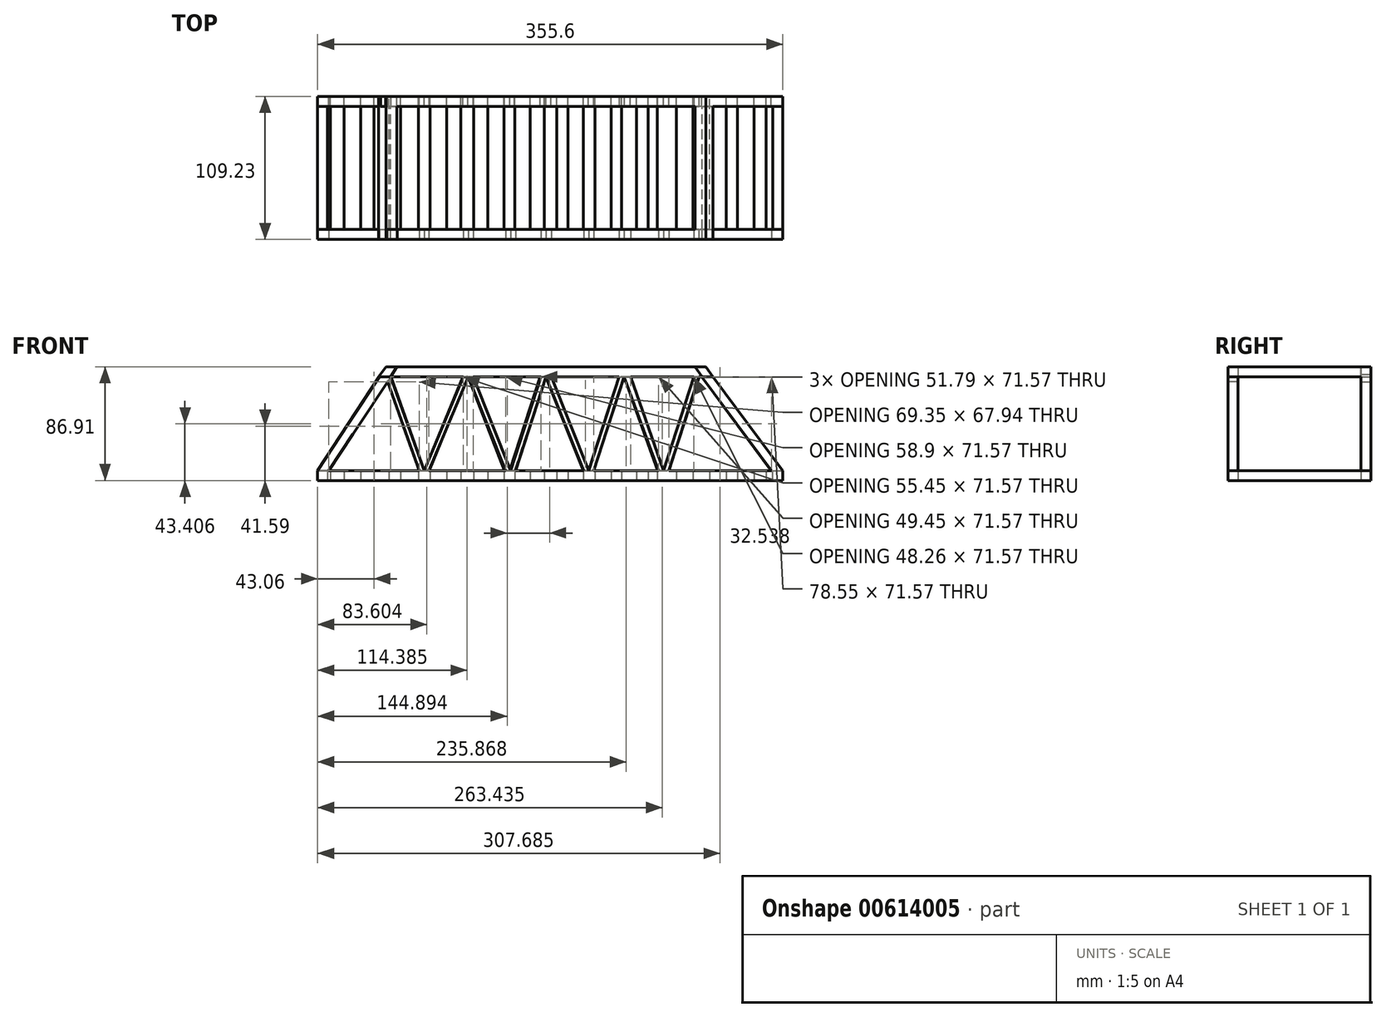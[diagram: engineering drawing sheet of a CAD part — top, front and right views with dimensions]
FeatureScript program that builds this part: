
annotation { "Feature Type Name" : "Feature", "Feature Type Description" : "" }
export const myFeature = defineFeature(function(context is Context, id is Id, definition is map)
    precondition{}
    {
        {
            var Q0;
            Q0=qCreatedBy(makeId("Front.planeOp"),FACE);
            var sketch = newSketch(context, id + "F0", { "sketchPlane" : qUnion([Q0])});
            skLineSegment(sketch, "E0.bottom", {"start": v(-81.44, 46.17) * mm, "end": v(274.16, 46.17) * mm});
            skLineSegment(sketch, "E0.top", {"start": v(-81.44, 38.55) * mm, "end": v(274.16, 38.55) * mm});
            skLineSegment(sketch, "E0.left", {"start": v(-81.44, 46.17) * mm, "end": v(-81.44, 38.55) * mm});
            skLineSegment(sketch, "E0.right", {"start": v(274.16, 46.17) * mm, "end": v(274.16, 38.55) * mm});
            skLineSegment(sketch, "E1.bottom", {"start": v(-81.44, -33.02) * mm, "end": v(274.16, -33.02) * mm});
            skLineSegment(sketch, "E1.top", {"start": v(-81.44, -40.64) * mm, "end": v(274.16, -40.64) * mm});
            skLineSegment(sketch, "E1.left", {"start": v(-81.44, -33.02) * mm, "end": v(-81.44, -40.64) * mm});
            skLineSegment(sketch, "E1.right", {"start": v(274.16, -33.02) * mm, "end": v(274.16, -40.64) * mm});
            skSolve(sketch);
        }
        {
            var Q0;
            Q0=makeQuery(id+"F0.imprint","IMPRINT",FACE,{"disambiguationData":[TD([[makeQuery(id+"F0.imprint","IMPRINT",EDGE,{"derivedFrom":sQuery(id+"F0.wireOp",EDGE,"E0.bottom")}),-1.0]])]});
            var Q1;
            Q1=makeQuery(id+"F0.imprint","IMPRINT",FACE,{"disambiguationData":[TD([[makeQuery(id+"F0.imprint","IMPRINT",EDGE,{"derivedFrom":sQuery(id+"F0.wireOp",EDGE,"E1.bottom")}),-1.0]])]});
            extrude(context, id + "F1", {"entities" : qUnion([Q0, Q1]), "depth" : 7.62 * mm, "offsetDistance" : 25.4 * mm});
        }
        {
            var Q0;
            Q0=makeQuery(id+"F1.opExtrude","SWEPT_FACE",FACE,{"disambiguationData":[OSD([sQuery(id+"F0.wireOp",EDGE,"E1.left")])]});
            var sketch = newSketch(context, id + "F2", { "sketchPlane" : qUnion([Q0])});
            skLineSegment(sketch, "E2.bottom", {"start": v(7.62, -33.02) * mm, "end": v(-101.6, -33.02) * mm});
            skLineSegment(sketch, "E2.top", {"start": v(7.62, -40.64) * mm, "end": v(-101.6, -40.64) * mm});
            skLineSegment(sketch, "E2.left", {"start": v(7.62, -33.02) * mm, "end": v(7.62, -40.64) * mm});
            skLineSegment(sketch, "E2.right", {"start": v(-101.6, -33.02) * mm, "end": v(-101.6, -40.64) * mm});
            skSolve(sketch);
        }
        {
            var Q0;
            Q0 = qSketchRegion(id + "F2", true);
            extrude(context, id + "F3", {"entities" : qUnion([Q0]), "operationType" : NewBodyOperationType.ADD, "oppositeDirection" : true, "depth" : 7.62 * mm, "offsetDistance" : 25.4 * mm});
        }
        {
            var Q0;
            Q0=makeQuery(id+"F1.opExtrude","CAP_FACE",FACE,{"disambiguationData":[OSD([sQuery(id+"F0.wireOp",EDGE,"E0.bottom"),sQuery(id+"F0.wireOp",EDGE,"E0.top"),sQuery(id+"F0.wireOp",EDGE,"E0.left"),sQuery(id+"F0.wireOp",EDGE,"E0.right")])],"isStart":true});
            var sketch = newSketch(context, id + "F4", { "sketchPlane" : qUnion([Q0])});
            skLineSegment(sketch, "E3.bottom", {"start": v(81.44, 46.17) * mm, "end": v(73.82, 46.17) * mm});
            skLineSegment(sketch, "E3.top", {"start": v(81.44, 38.55) * mm, "end": v(73.82, 38.55) * mm});
            skLineSegment(sketch, "E3.left", {"start": v(81.44, 46.17) * mm, "end": v(81.44, 38.55) * mm});
            skLineSegment(sketch, "E3.right", {"start": v(73.82, 46.17) * mm, "end": v(73.82, 38.55) * mm});
            skSolve(sketch);
        }
        {
            var Q0;
            Q0 = qSketchRegion(id + "F4", true);
            extrude(context, id + "F5", {"entities" : qUnion([Q0]), "operationType" : NewBodyOperationType.ADD, "depth" : 101.6 * mm, "offsetDistance" : 25.4 * mm});
        }
        {
            var Q0;
            Q0=makeQuery(id+"F5.opExtrude","SWEPT_FACE",FACE,{"disambiguationData":[OSD([sQuery(id+"F4.wireOp",EDGE,"E3.right")])]});
            var sketch = newSketch(context, id + "F6", { "sketchPlane" : qUnion([Q0])});
            skLineSegment(sketch, "E4.bottom", {"start": v(101.6, 46.17) * mm, "end": v(93.97, 46.17) * mm});
            skLineSegment(sketch, "E4.top", {"start": v(101.6, 38.55) * mm, "end": v(93.97, 38.55) * mm});
            skLineSegment(sketch, "E4.left", {"start": v(101.6, 46.17) * mm, "end": v(101.6, 38.55) * mm});
            skLineSegment(sketch, "E4.right", {"start": v(93.97, 46.17) * mm, "end": v(93.97, 38.55) * mm});
            skSolve(sketch);
        }
        {
            var Q0;
            Q0 = qSketchRegion(id + "F6", true);
            extrude(context, id + "F7", {"entities" : qUnion([Q0]), "operationType" : NewBodyOperationType.ADD, "depth" : 347.98 * mm, "offsetDistance" : 25.4 * mm});
        }
        {
            var Q0;
            Q0=makeQuery(id+"F1.opExtrude","CAP_FACE",FACE,{"disambiguationData":[OSD([sQuery(id+"F0.wireOp",EDGE,"E0.bottom"),sQuery(id+"F0.wireOp",EDGE,"E0.top"),sQuery(id+"F0.wireOp",EDGE,"E0.left"),sQuery(id+"F0.wireOp",EDGE,"E0.right")])],"isStart":true});
            var sketch = newSketch(context, id + "F8", { "sketchPlane" : qUnion([Q0])});
            skLineSegment(sketch, "E5.bottom", {"start": v(-274.16, 46.17) * mm, "end": v(-266.54, 46.17) * mm});
            skLineSegment(sketch, "E5.top", {"start": v(-274.16, 38.55) * mm, "end": v(-266.54, 38.55) * mm});
            skLineSegment(sketch, "E5.left", {"start": v(-274.16, 46.17) * mm, "end": v(-274.16, 38.55) * mm});
            skLineSegment(sketch, "E5.right", {"start": v(-266.54, 46.17) * mm, "end": v(-266.54, 38.55) * mm});
            skSolve(sketch);
        }
        {
            var Q0;
            Q0 = qSketchRegion(id + "F8", true);
            extrude(context, id + "F9", {"entities" : qUnion([Q0]), "operationType" : NewBodyOperationType.ADD, "depth" : 93.98 * mm, "offsetDistance" : 25.4 * mm});
        }
        {
            var Q0;
            Q0=makeQuery(id+"F1.opExtrude","CAP_FACE",FACE,{"disambiguationData":[OSD([sQuery(id+"F0.wireOp",EDGE,"E1.bottom"),sQuery(id+"F0.wireOp",EDGE,"E1.top"),sQuery(id+"F0.wireOp",EDGE,"E1.left"),sQuery(id+"F0.wireOp",EDGE,"E1.right")])],"isStart":true});
            var sketch = newSketch(context, id + "F10", { "sketchPlane" : qUnion([Q0])});
            skLineSegment(sketch, "E6.bottom", {"start": v(-274.16, -40.64) * mm, "end": v(-266.54, -40.64) * mm});
            skLineSegment(sketch, "E6.top", {"start": v(-274.16, -33.02) * mm, "end": v(-266.54, -33.02) * mm});
            skLineSegment(sketch, "E6.left", {"start": v(-274.16, -40.64) * mm, "end": v(-274.16, -33.02) * mm});
            skLineSegment(sketch, "E6.right", {"start": v(-266.54, -40.64) * mm, "end": v(-266.54, -33.02) * mm});
            skSolve(sketch);
        }
        {
            var Q0;
            Q0 = qSketchRegion(id + "F10", true);
            extrude(context, id + "F11", {"entities" : qUnion([Q0]), "operationType" : NewBodyOperationType.ADD, "depth" : 101.6 * mm, "offsetDistance" : 25.4 * mm});
        }
        {
            var Q0;
            Q0=makeQuery(id+"F11.opExtrude","SWEPT_FACE",FACE,{"disambiguationData":[OSD([sQuery(id+"F10.wireOp",EDGE,"E6.right")])]});
            var sketch = newSketch(context, id + "F12", { "sketchPlane" : qUnion([Q0])});
            skLineSegment(sketch, "E7.bottom", {"start": v(-101.6, -33.02) * mm, "end": v(-93.98, -33.02) * mm});
            skLineSegment(sketch, "E7.top", {"start": v(-101.6, -40.64) * mm, "end": v(-93.98, -40.64) * mm});
            skLineSegment(sketch, "E7.left", {"start": v(-101.6, -33.02) * mm, "end": v(-101.6, -40.64) * mm});
            skLineSegment(sketch, "E7.right", {"start": v(-93.98, -33.02) * mm, "end": v(-93.98, -40.64) * mm});
            skSolve(sketch);
        }
        {
            var Q0;
            Q0 = qSketchRegion(id + "F12", true);
            extrude(context, id + "F13", {"entities" : qUnion([Q0]), "operationType" : NewBodyOperationType.ADD, "depth" : 340.36 * mm, "offsetDistance" : 25.4 * mm});
        }
        {
            var Q0;
            Q0=makeQuery(id+"F1.opExtrude","CAP_FACE",FACE,{"disambiguationData":[OSD([sQuery(id+"F0.wireOp",EDGE,"E1.bottom"),sQuery(id+"F0.wireOp",EDGE,"E1.top"),sQuery(id+"F0.wireOp",EDGE,"E1.left"),sQuery(id+"F0.wireOp",EDGE,"E1.right")])],"isStart":false});
            var sketch = newSketch(context, id + "F14", { "sketchPlane" : qUnion([Q0])});
            skLineSegment(sketch, "E8", {"start": v(-81.44, -33.02) * mm, "end": v(-28.78, 46.35) * mm});
            skLineSegment(sketch, "E9", {"start": v(-28.78, 46.35) * mm, "end": v(-20.39, 46.35) * mm});
            skLineSegment(sketch, "E10", {"start": v(-20.39, 46.35) * mm, "end": v(-73.05, -33.02) * mm});
            skLineSegment(sketch, "E11", {"start": v(-73.05, -33.02) * mm, "end": v(-81.44, -33.02) * mm});
            skSolve(sketch);
        }
        {
            var Q0;
            Q0=makeQuery(id+"F14.imprint","IMPRINT",FACE,{"disambiguationData":[TD([[makeQuery(id+"F14.imprint","IMPRINT",EDGE,{"derivedFrom":sQuery(id+"F14.wireOp",EDGE,"E8")}),-1.0]])]});
            extrude(context, id + "F15", {"entities" : qUnion([Q0]), "oppositeDirection" : true, "depth" : 7.62 * mm, "offsetDistance" : 25.4 * mm});
        }
        {
            var Q0;
            Q0=makeQuery(id+"F15.opExtrude","SWEPT_BODY",BODY,{"disambiguationData":[OSD([sQuery(id+"F14.wireOp",EDGE,"E8"),sQuery(id+"F14.wireOp",EDGE,"E9"),sQuery(id+"F14.wireOp",EDGE,"E10"),sQuery(id+"F14.wireOp",EDGE,"E11")])]});
            var Q1;
            Q1=makeQuery(id+"F1.opExtrude","SWEPT_BODY",BODY,{"disambiguationData":[OSD([sQuery(id+"F0.wireOp",EDGE,"E0.bottom"),sQuery(id+"F0.wireOp",EDGE,"E0.top"),sQuery(id+"F0.wireOp",EDGE,"E0.left"),sQuery(id+"F0.wireOp",EDGE,"E0.right")])]});
            booleanBodies(context, id + "F16", {"operationType" : BooleanOperationType.UNION, "tools" : qUnion([Q0, Q1])});
        }
        {
            var Q0;
            Q0=makeQuery(id+"F16.opBoolean","MERGE",FACE,{"derivedFrom":[makeQuery(id+"F1.opExtrude","CAP_FACE",FACE,{"disambiguationData":[OSD([sQuery(id+"F0.wireOp",EDGE,"E0.bottom"),sQuery(id+"F0.wireOp",EDGE,"E0.top"),sQuery(id+"F0.wireOp",EDGE,"E0.left"),sQuery(id+"F0.wireOp",EDGE,"E0.right")])],"isStart":false}),makeQuery(id+"F15.opExtrude","CAP_FACE",FACE,{"disambiguationData":[OSD([sQuery(id+"F14.wireOp",EDGE,"E8"),sQuery(id+"F14.wireOp",EDGE,"E9"),sQuery(id+"F14.wireOp",EDGE,"E10"),sQuery(id+"F14.wireOp",EDGE,"E11")])],"isStart":true})]});
            var sketch = newSketch(context, id + "F17", { "sketchPlane" : qUnion([Q0])});
            skLineSegment(sketch, "E12", {"start": v(-33.95, 38.55) * mm, "end": v(-28.78, 46.35) * mm});
            skLineSegment(sketch, "E13", {"start": v(-28.78, 46.35) * mm, "end": v(-81.44, 46.17) * mm});
            skLineSegment(sketch, "E14", {"start": v(-81.44, 46.17) * mm, "end": v(-81.44, 38.55) * mm});
            skLineSegment(sketch, "E15", {"start": v(-81.44, 38.55) * mm, "end": v(-33.95, 38.55) * mm});
            skSolve(sketch);
        }
        {
            var Q0;
            Q0=makeQuery(id+"F13.boolean.opBoolean","MERGE",FACE,{"derivedFrom":[makeQuery(id+"F3.opExtrude","SWEPT_FACE",FACE,{"disambiguationData":[OSD([sQuery(id+"F2.wireOp",EDGE,"E2.right")])]}),makeQuery(id+"F11.opExtrude","CAP_FACE",FACE,{"disambiguationData":[OSD([sQuery(id+"F10.wireOp",EDGE,"E6.bottom"),sQuery(id+"F10.wireOp",EDGE,"E6.top"),sQuery(id+"F10.wireOp",EDGE,"E6.left"),sQuery(id+"F10.wireOp",EDGE,"E6.right")])],"isStart":false}),makeQuery(id+"F13.opExtrude","SWEPT_FACE",FACE,{"disambiguationData":[OSD([sQuery(id+"F12.wireOp",EDGE,"E7.left")])]})]});
            var sketch = newSketch(context, id + "F18", { "sketchPlane" : qUnion([Q0])});
            skLineSegment(sketch, "E16", {"start": v(81.44, -33.02) * mm, "end": v(29.7, 45.88) * mm});
            skLineSegment(sketch, "E17", {"start": v(29.7, 45.88) * mm, "end": v(20.94, 45.88) * mm});
            skLineSegment(sketch, "E18", {"start": v(20.94, 45.88) * mm, "end": v(72.92, -33.02) * mm});
            skLineSegment(sketch, "E19", {"start": v(72.92, -33.02) * mm, "end": v(81.44, -33.02) * mm});
            skSolve(sketch);
        }
        {
            var Q0;
            Q0 = qSketchRegion(id + "F18", true);
            extrude(context, id + "F19", {"entities" : qUnion([Q0]), "oppositeDirection" : true, "depth" : 7.62 * mm, "offsetDistance" : 25.4 * mm});
        }
        {
            var Q0;
            Q0=makeQuery(id+"F17.imprint","IMPRINT",FACE,{"disambiguationData":[TD([[makeQuery(id+"F17.imprint","IMPRINT",EDGE,{"derivedFrom":sQuery(id+"F17.wireOp",EDGE,"E14")}),1.0]])]});
            var sketch = newSketch(context, id + "F20", { "sketchPlane" : qUnion([Q0])});
            skLineSegment(sketch, "E20", {"start": v(-28.75, 46.61) * mm, "end": v(-36.09, 36.61) * mm});
            skLineSegment(sketch, "E21", {"start": v(-36.09, 36.61) * mm, "end": v(-88.6, 34.11) * mm});
            skLineSegment(sketch, "E22", {"start": v(-88.6, 34.11) * mm, "end": v(-88.6, 49.28) * mm});
            skLineSegment(sketch, "E23", {"start": v(-88.6, 49.28) * mm, "end": v(-28.92, 49.28) * mm});
            skLineSegment(sketch, "E24", {"start": v(-28.92, 49.28) * mm, "end": v(-19.25, 49.28) * mm});
            skLineSegment(sketch, "E25", {"start": v(-19.25, 49.28) * mm, "end": v(-19.25, 46.27) * mm});
            skLineSegment(sketch, "E26", {"start": v(-19.25, 46.27) * mm, "end": v(-29, 46.27) * mm});
            skSolve(sketch);
        }
        {
            var Q0;
            Q0 = qSketchRegion(id + "F20", true);
            extrude(context, id + "F21", {"entities" : qUnion([Q0]), "operationType" : NewBodyOperationType.REMOVE, "oppositeDirection" : true, "depth" : 127 * mm, "offsetDistance" : 25.4 * mm});
        }
        {
            var Q0;
            Q0=makeQuery(id+"F17.imprint","IMPRINT",FACE,{"disambiguationData":[TD([[makeQuery(id+"F17.imprint","IMPRINT",EDGE,{"derivedFrom":sQuery(id+"F17.wireOp",EDGE,"E14")}),1.0]])]});
            extrude(context, id + "F22", {"entities" : qUnion([Q0]), "operationType" : NewBodyOperationType.REMOVE, "oppositeDirection" : true, "depth" : 25.4 * mm, "offsetDistance" : 25.4 * mm});
        }
        {
            var Q0;
            Q0=makeQuery(id+"F1.opExtrude","CAP_FACE",FACE,{"disambiguationData":[OSD([sQuery(id+"F0.wireOp",EDGE,"E1.bottom"),sQuery(id+"F0.wireOp",EDGE,"E1.top"),sQuery(id+"F0.wireOp",EDGE,"E1.left"),sQuery(id+"F0.wireOp",EDGE,"E1.right")])],"isStart":false});
            var sketch = newSketch(context, id + "F23", { "sketchPlane" : qUnion([Q0])});
            skLineSegment(sketch, "E27", {"start": v(274.16, -33.02) * mm, "end": v(214.97, 46.19) * mm});
            skLineSegment(sketch, "E28", {"start": v(214.97, 46.19) * mm, "end": v(206.33, 46.19) * mm});
            skLineSegment(sketch, "E29", {"start": v(206.33, 46.19) * mm, "end": v(265.52, -33.02) * mm});
            skLineSegment(sketch, "E30", {"start": v(265.52, -33.02) * mm, "end": v(274.16, -33.02) * mm});
            skSolve(sketch);
        }
        {
            var Q0;
            Q0 = qSketchRegion(id + "F23", true);
            extrude(context, id + "F24", {"entities" : qUnion([Q0]), "operationType" : NewBodyOperationType.ADD, "oppositeDirection" : true, "depth" : 7.62 * mm, "offsetDistance" : 25.4 * mm});
        }
        {
            var Q0;
            Q0=makeQuery(id+"F13.boolean.opBoolean","MERGE",FACE,{"derivedFrom":[makeQuery(id+"F3.opExtrude","SWEPT_FACE",FACE,{"disambiguationData":[OSD([sQuery(id+"F2.wireOp",EDGE,"E2.right")])]}),makeQuery(id+"F11.opExtrude","CAP_FACE",FACE,{"disambiguationData":[OSD([sQuery(id+"F10.wireOp",EDGE,"E6.bottom"),sQuery(id+"F10.wireOp",EDGE,"E6.top"),sQuery(id+"F10.wireOp",EDGE,"E6.left"),sQuery(id+"F10.wireOp",EDGE,"E6.right")])],"isStart":false}),makeQuery(id+"F13.opExtrude","SWEPT_FACE",FACE,{"disambiguationData":[OSD([sQuery(id+"F12.wireOp",EDGE,"E7.left")])]})]});
            var sketch = newSketch(context, id + "F25", { "sketchPlane" : qUnion([Q0])});
            skLineSegment(sketch, "E31", {"start": v(-274.16, -33.02) * mm, "end": v(-214.97, 46.51) * mm});
            skLineSegment(sketch, "E32", {"start": v(-214.97, 46.51) * mm, "end": v(-206.28, 46.51) * mm});
            skLineSegment(sketch, "E33", {"start": v(-206.28, 46.51) * mm, "end": v(-265.18, -33.02) * mm});
            skLineSegment(sketch, "E34", {"start": v(-265.18, -33.02) * mm, "end": v(-274.16, -33.02) * mm});
            skSolve(sketch);
        }
        {
            var Q0;
            Q0 = qSketchRegion(id + "F25", true);
            extrude(context, id + "F26", {"entities" : qUnion([Q0]), "operationType" : NewBodyOperationType.ADD, "oppositeDirection" : true, "depth" : 7.62 * mm, "offsetDistance" : 25.4 * mm});
        }
        {
            var Q0;
            Q0=makeQuery(id+"F26.boolean.opBoolean","MERGE",FACE,{"derivedFrom":[makeQuery(id+"F13.boolean.opBoolean","MERGE",FACE,{"derivedFrom":[makeQuery(id+"F3.opExtrude","SWEPT_FACE",FACE,{"disambiguationData":[OSD([sQuery(id+"F2.wireOp",EDGE,"E2.right")])]}),makeQuery(id+"F11.opExtrude","CAP_FACE",FACE,{"disambiguationData":[OSD([sQuery(id+"F10.wireOp",EDGE,"E6.bottom"),sQuery(id+"F10.wireOp",EDGE,"E6.top"),sQuery(id+"F10.wireOp",EDGE,"E6.left"),sQuery(id+"F10.wireOp",EDGE,"E6.right")])],"isStart":false}),makeQuery(id+"F13.opExtrude","SWEPT_FACE",FACE,{"disambiguationData":[OSD([sQuery(id+"F12.wireOp",EDGE,"E7.left")])]})]}),makeQuery(id+"F7.boolean.opBoolean","MERGE",FACE,{"derivedFrom":[makeQuery(id+"F5.opExtrude","CAP_FACE",FACE,{"disambiguationData":[OSD([sQuery(id+"F4.wireOp",EDGE,"E3.bottom"),sQuery(id+"F4.wireOp",EDGE,"E3.top"),sQuery(id+"F4.wireOp",EDGE,"E3.left"),sQuery(id+"F4.wireOp",EDGE,"E3.right")])],"isStart":false}),makeQuery(id+"F7.opExtrude","SWEPT_FACE",FACE,{"disambiguationData":[OSD([sQuery(id+"F6.wireOp",EDGE,"E4.left")])]})]}),makeQuery(id+"F26.opExtrude","CAP_FACE",FACE,{"disambiguationData":[OSD([sQuery(id+"F25.wireOp",EDGE,"E31"),sQuery(id+"F25.wireOp",EDGE,"E32"),sQuery(id+"F25.wireOp",EDGE,"E33"),sQuery(id+"F25.wireOp",EDGE,"E34")])],"isStart":true})]});
            var sketch = newSketch(context, id + "F27", { "sketchPlane" : qUnion([Q0])});
            skLineSegment(sketch, "E35", {"start": v(-220.9, 38.55) * mm, "end": v(-215.22, 46.17) * mm});
            skLineSegment(sketch, "E36", {"start": v(-215.22, 46.17) * mm, "end": v(-206.2, 46.17) * mm});
            skLineSegment(sketch, "E37", {"start": v(-206.2, 46.17) * mm, "end": v(-206.2, 46.76) * mm});
            skLineSegment(sketch, "E38", {"start": v(-206.2, 46.76) * mm, "end": v(-277.38, 46.17) * mm});
            skLineSegment(sketch, "E39", {"start": v(-277.38, 46.17) * mm, "end": v(-277.38, 38.55) * mm});
            skLineSegment(sketch, "E40", {"start": v(-277.38, 38.55) * mm, "end": v(-220.9, 38.55) * mm});
            skSolve(sketch);
        }
        {
            var Q0;
            Q0 = qSketchRegion(id + "F27", true);
            extrude(context, id + "F28", {"entities" : qUnion([Q0]), "operationType" : NewBodyOperationType.REMOVE, "oppositeDirection" : true, "depth" : 127 * mm, "offsetDistance" : 25.4 * mm});
        }
        {
            var Q0;
            Q0=makeQuery(id+"F24.boolean.opBoolean","MERGE",FACE,{"derivedFrom":[makeQuery(id+"F1.opExtrude","CAP_FACE",FACE,{"disambiguationData":[OSD([sQuery(id+"F0.wireOp",EDGE,"E1.bottom"),sQuery(id+"F0.wireOp",EDGE,"E1.top"),sQuery(id+"F0.wireOp",EDGE,"E1.left"),sQuery(id+"F0.wireOp",EDGE,"E1.right")])],"isStart":false}),makeQuery(id+"F16.opBoolean","MERGE",FACE,{"derivedFrom":[makeQuery(id+"F1.opExtrude","CAP_FACE",FACE,{"disambiguationData":[OSD([sQuery(id+"F0.wireOp",EDGE,"E0.bottom"),sQuery(id+"F0.wireOp",EDGE,"E0.top"),sQuery(id+"F0.wireOp",EDGE,"E0.left"),sQuery(id+"F0.wireOp",EDGE,"E0.right")])],"isStart":false}),makeQuery(id+"F15.opExtrude","CAP_FACE",FACE,{"disambiguationData":[OSD([sQuery(id+"F14.wireOp",EDGE,"E8"),sQuery(id+"F14.wireOp",EDGE,"E9"),sQuery(id+"F14.wireOp",EDGE,"E10"),sQuery(id+"F14.wireOp",EDGE,"E11")])],"isStart":true})]}),makeQuery(id+"F24.opExtrude","CAP_FACE",FACE,{"disambiguationData":[OSD([sQuery(id+"F23.wireOp",EDGE,"E27"),sQuery(id+"F23.wireOp",EDGE,"E28"),sQuery(id+"F23.wireOp",EDGE,"E29"),sQuery(id+"F23.wireOp",EDGE,"E30")])],"isStart":true})]});
            var sketch = newSketch(context, id + "F29", { "sketchPlane" : qUnion([Q0])});
            skLineSegment(sketch, "E41", {"start": v(3.5, -33.02) * mm, "end": v(33.75, 38.55) * mm});
            skLineSegment(sketch, "E42", {"start": v(33.75, 38.55) * mm, "end": v(29.89, 38.55) * mm});
            skLineSegment(sketch, "E43", {"start": v(33.75, 38.55) * mm, "end": v(62.4, -33.02) * mm});
            skLineSegment(sketch, "E44", {"start": v(62.4, -33.02) * mm, "end": v(66.2, -33.02) * mm});
            skLineSegment(sketch, "E45", {"start": v(66.2, -33.02) * mm, "end": v(37.56, 38.55) * mm});
            skLineSegment(sketch, "E46", {"start": v(37.56, 38.55) * mm, "end": v(33.75, 38.55) * mm});
            skLineSegment(sketch, "E47", {"start": v(66.2, -33.02) * mm, "end": v(89.35, 38.55) * mm});
            skLineSegment(sketch, "E48", {"start": v(89.35, 38.55) * mm, "end": v(93.24, 38.55) * mm});
            skLineSegment(sketch, "E49", {"start": v(93.24, 38.55) * mm, "end": v(70.1, -33.02) * mm});
            skLineSegment(sketch, "E50", {"start": v(70.1, -33.02) * mm, "end": v(66.2, -33.02) * mm});
            skLineSegment(sketch, "E51", {"start": v(93.24, 38.55) * mm, "end": v(121.88, -33.02) * mm});
            skLineSegment(sketch, "E52", {"start": v(121.88, -33.02) * mm, "end": v(125.9, -33.02) * mm});
            skLineSegment(sketch, "E53", {"start": v(125.9, -33.02) * mm, "end": v(97.25, 38.55) * mm});
            skLineSegment(sketch, "E54", {"start": v(97.25, 38.55) * mm, "end": v(93.24, 38.55) * mm});
            skLineSegment(sketch, "E55", {"start": v(29.89, 38.55) * mm, "end": v(0, -33.02) * mm});
            skLineSegment(sketch, "E56", {"start": v(0, -33.02) * mm, "end": v(-25.56, 38.55) * mm});
            skLineSegment(sketch, "E57", {"start": v(-25.56, 38.55) * mm, "end": v(-27.97, 34.92) * mm});
            skLineSegment(sketch, "E58", {"start": v(-27.97, 34.92) * mm, "end": v(-3.7, -33.02) * mm});
            skLineSegment(sketch, "E59", {"start": v(-3.7, -33.02) * mm, "end": v(0, -33.02) * mm});
            skLineSegment(sketch, "E60", {"start": v(125.9, -33.02) * mm, "end": v(149.03, 38.55) * mm});
            skLineSegment(sketch, "E61", {"start": v(149.03, 38.55) * mm, "end": v(152.84, 38.55) * mm});
            skLineSegment(sketch, "E62", {"start": v(152.84, 38.55) * mm, "end": v(129.7, -33.02) * mm});
            skLineSegment(sketch, "E63", {"start": v(129.7, -33.02) * mm, "end": v(125.9, -33.02) * mm});
            skLineSegment(sketch, "E64", {"start": v(152.84, 38.55) * mm, "end": v(179.15, -33.02) * mm});
            skLineSegment(sketch, "E65", {"start": v(179.15, -33.02) * mm, "end": v(182.98, -33.02) * mm});
            skLineSegment(sketch, "E66", {"start": v(182.98, -33.02) * mm, "end": v(157.86, 38.55) * mm});
            skLineSegment(sketch, "E67", {"start": v(157.86, 38.55) * mm, "end": v(152.84, 38.55) * mm});
            skLineSegment(sketch, "E68", {"start": v(182.98, -33.02) * mm, "end": v(206.12, 38.55) * mm});
            skLineSegment(sketch, "E69", {"start": v(206.12, 38.55) * mm, "end": v(210.11, 38.55) * mm});
            skLineSegment(sketch, "E70", {"start": v(210.11, 38.55) * mm, "end": v(186.97, -33.02) * mm});
            skLineSegment(sketch, "E71", {"start": v(186.97, -33.02) * mm, "end": v(182.98, -33.02) * mm});
            skLineSegment(sketch, "E72", {"start": v(157.86, 38.55) * mm, "end": v(206.12, 38.55) * mm});
            skSolve(sketch);
        }
        {
            var Q0;
            Q0=makeQuery(id+"F29.imprint","IMPRINT",FACE,{"disambiguationData":[TD([[makeQuery(id+"F29.imprint","IMPRINT",EDGE,{"derivedFrom":sQuery(id+"F29.wireOp",EDGE,"E56")}),1.0]])]});
            var Q1;
            {var subQ0=sQuery(id+"F29.wireOp",EDGE,"E41");Q1=makeQuery(id+"F29.imprint","IMPRINT",FACE,{"disambiguationData":[TD([[makeQuery(id+"F29.imprint","IMPRINT",EDGE,{"derivedFrom":subQ0}),1.0]])]});}
            var Q2;
            Q2=makeQuery(id+"F29.imprint","IMPRINT",FACE,{"disambiguationData":[TD([[makeQuery(id+"F29.imprint","IMPRINT",EDGE,{"derivedFrom":sQuery(id+"F29.wireOp",EDGE,"E43")}),1.0]])]});
            var Q3;
            Q3=makeQuery(id+"F29.imprint","IMPRINT",FACE,{"disambiguationData":[TD([[makeQuery(id+"F29.imprint","IMPRINT",EDGE,{"derivedFrom":sQuery(id+"F29.wireOp",EDGE,"E47")}),-1.0]])]});
            var Q4;
            Q4=makeQuery(id+"F29.imprint","IMPRINT",FACE,{"disambiguationData":[TD([[makeQuery(id+"F29.imprint","IMPRINT",EDGE,{"derivedFrom":sQuery(id+"F29.wireOp",EDGE,"E51")}),1.0]])]});
            var Q5;
            Q5=makeQuery(id+"F29.imprint","IMPRINT",FACE,{"disambiguationData":[TD([[makeQuery(id+"F29.imprint","IMPRINT",EDGE,{"derivedFrom":sQuery(id+"F29.wireOp",EDGE,"E60")}),-1.0]])]});
            var Q6;
            Q6=makeQuery(id+"F29.imprint","IMPRINT",FACE,{"disambiguationData":[TD([[makeQuery(id+"F29.imprint","IMPRINT",EDGE,{"derivedFrom":sQuery(id+"F29.wireOp",EDGE,"E68")}),-1.0]])]});
            var Q7;
            Q7=makeQuery(id+"F29.imprint","IMPRINT",FACE,{"disambiguationData":[TD([[makeQuery(id+"F29.imprint","IMPRINT",EDGE,{"derivedFrom":sQuery(id+"F29.wireOp",EDGE,"E64")}),1.0]])]});
            extrude(context, id + "F30", {"entities" : qUnion([Q0, Q1, Q2, Q3, Q4, Q5, Q6, Q7]), "operationType" : NewBodyOperationType.ADD, "oppositeDirection" : true, "depth" : 7.62 * mm, "offsetDistance" : 25.4 * mm});
        }
        {
            var Q0;
            Q0=makeQuery(id+"F26.boolean.opBoolean","MERGE",FACE,{"derivedFrom":[makeQuery(id+"F13.boolean.opBoolean","MERGE",FACE,{"derivedFrom":[makeQuery(id+"F3.opExtrude","SWEPT_FACE",FACE,{"disambiguationData":[OSD([sQuery(id+"F2.wireOp",EDGE,"E2.right")])]}),makeQuery(id+"F11.opExtrude","CAP_FACE",FACE,{"disambiguationData":[OSD([sQuery(id+"F10.wireOp",EDGE,"E6.bottom"),sQuery(id+"F10.wireOp",EDGE,"E6.top"),sQuery(id+"F10.wireOp",EDGE,"E6.left"),sQuery(id+"F10.wireOp",EDGE,"E6.right")])],"isStart":false}),makeQuery(id+"F13.opExtrude","SWEPT_FACE",FACE,{"disambiguationData":[OSD([sQuery(id+"F12.wireOp",EDGE,"E7.left")])]})]}),makeQuery(id+"F7.boolean.opBoolean","MERGE",FACE,{"derivedFrom":[makeQuery(id+"F5.opExtrude","CAP_FACE",FACE,{"disambiguationData":[OSD([sQuery(id+"F4.wireOp",EDGE,"E3.bottom"),sQuery(id+"F4.wireOp",EDGE,"E3.top"),sQuery(id+"F4.wireOp",EDGE,"E3.left"),sQuery(id+"F4.wireOp",EDGE,"E3.right")])],"isStart":false}),makeQuery(id+"F7.opExtrude","SWEPT_FACE",FACE,{"disambiguationData":[OSD([sQuery(id+"F6.wireOp",EDGE,"E4.left")])]})]}),makeQuery(id+"F26.opExtrude","CAP_FACE",FACE,{"disambiguationData":[OSD([sQuery(id+"F25.wireOp",EDGE,"E31"),sQuery(id+"F25.wireOp",EDGE,"E32"),sQuery(id+"F25.wireOp",EDGE,"E33"),sQuery(id+"F25.wireOp",EDGE,"E34")])],"isStart":true})]});
            var sketch = newSketch(context, id + "F31", { "sketchPlane" : qUnion([Q0])});
            skLineSegment(sketch, "E73", {"start": v(-206.56, 38.55) * mm, "end": v(-210.37, 38.55) * mm});
            skLineSegment(sketch, "E74", {"start": v(-210.37, 38.55) * mm, "end": v(-186.97, -33.02) * mm});
            skLineSegment(sketch, "E75", {"start": v(-186.97, -33.02) * mm, "end": v(-183.03, -33.02) * mm});
            skLineSegment(sketch, "E76", {"start": v(-183.03, -33.02) * mm, "end": v(-206.56, 38.55) * mm});
            skLineSegment(sketch, "E77", {"start": v(-157.55, 38.55) * mm, "end": v(-183.03, -33.02) * mm});
            skLineSegment(sketch, "E78", {"start": v(-178.6, -33.02) * mm, "end": v(-152.98, 38.55) * mm});
            skLineSegment(sketch, "E79", {"start": v(-152.98, 38.55) * mm, "end": v(-157.55, 38.55) * mm});
            skLineSegment(sketch, "E80", {"start": v(-152.98, 38.55) * mm, "end": v(-149.17, 38.55) * mm});
            skLineSegment(sketch, "E81", {"start": v(-149.17, 38.55) * mm, "end": v(-125.64, -33.02) * mm});
            skLineSegment(sketch, "E82", {"start": v(-125.64, -33.02) * mm, "end": v(-129.58, -33.02) * mm});
            skLineSegment(sketch, "E83", {"start": v(-129.58, -33.02) * mm, "end": v(-152.98, 38.55) * mm});
            skLineSegment(sketch, "E84", {"start": v(-97.01, 38.55) * mm, "end": v(-125.64, -33.02) * mm});
            skLineSegment(sketch, "E85", {"start": v(-121.7, -33.02) * mm, "end": v(-93.07, 38.55) * mm});
            skLineSegment(sketch, "E86", {"start": v(-93.07, 38.55) * mm, "end": v(-97.01, 38.55) * mm});
            skLineSegment(sketch, "E87", {"start": v(-93.07, 38.55) * mm, "end": v(-88.75, 38.55) * mm});
            skLineSegment(sketch, "E88", {"start": v(-88.75, 38.55) * mm, "end": v(-65.36, -33.02) * mm});
            skLineSegment(sketch, "E89", {"start": v(-65.36, -33.02) * mm, "end": v(-69.17, -33.02) * mm});
            skLineSegment(sketch, "E90", {"start": v(-69.17, -33.02) * mm, "end": v(-93.07, 38.55) * mm});
            skLineSegment(sketch, "E91", {"start": v(-65.36, -33.02) * mm, "end": v(-61.55, -33.02) * mm});
            skLineSegment(sketch, "E92", {"start": v(-61.55, -33.02) * mm, "end": v(-33.53, 38.55) * mm});
            skLineSegment(sketch, "E93", {"start": v(-33.53, 38.55) * mm, "end": v(-37.47, 38.55) * mm});
            skLineSegment(sketch, "E94", {"start": v(-37.47, 38.55) * mm, "end": v(-65.36, -33.02) * mm});
            skLineSegment(sketch, "E95", {"start": v(-33.53, 38.55) * mm, "end": v(-29.72, 38.55) * mm});
            skLineSegment(sketch, "E96", {"start": v(-29.72, 38.55) * mm, "end": v(0, -33.02) * mm});
            skLineSegment(sketch, "E97", {"start": v(0, -33.02) * mm, "end": v(-3.81, -33.02) * mm});
            skLineSegment(sketch, "E98", {"start": v(-3.8, -33.02) * mm, "end": v(-33.53, 38.55) * mm});
            skLineSegment(sketch, "E99", {"start": v(0, -33.02) * mm, "end": v(25.34, 38.55) * mm});
            skLineSegment(sketch, "E100", {"start": v(25.34, 38.55) * mm, "end": v(27.87, 34.94) * mm});
            skLineSegment(sketch, "E101", {"start": v(27.87, 34.94) * mm, "end": v(3.8, -33.02) * mm});
            skLineSegment(sketch, "E102", {"start": v(3.8, -33.02) * mm, "end": v(0, -33.02) * mm});
            skSolve(sketch);
        }
        {
            var Q0;
            Q0=makeQuery(id+"F31.imprint","IMPRINT",FACE,{"disambiguationData":[TD([[makeQuery(id+"F31.imprint","IMPRINT",EDGE,{"derivedFrom":sQuery(id+"F31.wireOp",EDGE,"E73")}),1.0]])]});
            var Q1;
            {var subQ0=sQuery(id+"F31.wireOp",EDGE,"E77");Q1=makeQuery(id+"F31.imprint","IMPRINT",FACE,{"disambiguationData":[TD([[makeQuery(id+"F31.imprint","IMPRINT",EDGE,{"derivedFrom":subQ0}),1.0]])]});}
            var Q2;
            Q2=makeQuery(id+"F31.imprint","IMPRINT",FACE,{"disambiguationData":[TD([[makeQuery(id+"F31.imprint","IMPRINT",EDGE,{"derivedFrom":sQuery(id+"F31.wireOp",EDGE,"E80")}),1.0]])]});
            var Q3;
            {var subQ0=sQuery(id+"F31.wireOp",EDGE,"E84");Q3=makeQuery(id+"F31.imprint","IMPRINT",FACE,{"disambiguationData":[TD([[makeQuery(id+"F31.imprint","IMPRINT",EDGE,{"derivedFrom":subQ0}),1.0]])]});}
            var Q4;
            Q4=makeQuery(id+"F31.imprint","IMPRINT",FACE,{"disambiguationData":[TD([[makeQuery(id+"F31.imprint","IMPRINT",EDGE,{"derivedFrom":sQuery(id+"F31.wireOp",EDGE,"E87")}),1.0]])]});
            var Q5;
            Q5=makeQuery(id+"F31.imprint","IMPRINT",FACE,{"disambiguationData":[TD([[makeQuery(id+"F31.imprint","IMPRINT",EDGE,{"derivedFrom":sQuery(id+"F31.wireOp",EDGE,"E91")}),1.0]])]});
            var Q6;
            Q6=makeQuery(id+"F31.imprint","IMPRINT",FACE,{"disambiguationData":[TD([[makeQuery(id+"F31.imprint","IMPRINT",EDGE,{"derivedFrom":sQuery(id+"F31.wireOp",EDGE,"E95")}),1.0]])]});
            var Q7;
            Q7=makeQuery(id+"F31.imprint","IMPRINT",FACE,{"disambiguationData":[TD([[makeQuery(id+"F31.imprint","IMPRINT",EDGE,{"derivedFrom":sQuery(id+"F31.wireOp",EDGE,"E99")}),-1.0]])]});
            extrude(context, id + "F32", {"entities" : qUnion([Q0, Q1, Q2, Q3, Q4, Q5, Q6, Q7]), "oppositeDirection" : true, "depth" : 7.62 * mm, "offsetDistance" : 25.4 * mm});
        }
        {
            var Q0;
            Q0=makeQuery(id+"F26.boolean.opBoolean","MERGE",FACE,{"derivedFrom":[makeQuery(id+"F13.boolean.opBoolean","MERGE",FACE,{"derivedFrom":[makeQuery(id+"F3.opExtrude","SWEPT_FACE",FACE,{"disambiguationData":[OSD([sQuery(id+"F2.wireOp",EDGE,"E2.right")])]}),makeQuery(id+"F11.opExtrude","CAP_FACE",FACE,{"disambiguationData":[OSD([sQuery(id+"F10.wireOp",EDGE,"E6.bottom"),sQuery(id+"F10.wireOp",EDGE,"E6.top"),sQuery(id+"F10.wireOp",EDGE,"E6.left"),sQuery(id+"F10.wireOp",EDGE,"E6.right")])],"isStart":false}),makeQuery(id+"F13.opExtrude","SWEPT_FACE",FACE,{"disambiguationData":[OSD([sQuery(id+"F12.wireOp",EDGE,"E7.left")])]})]}),makeQuery(id+"F7.boolean.opBoolean","MERGE",FACE,{"derivedFrom":[makeQuery(id+"F5.opExtrude","CAP_FACE",FACE,{"disambiguationData":[OSD([sQuery(id+"F4.wireOp",EDGE,"E3.bottom"),sQuery(id+"F4.wireOp",EDGE,"E3.top"),sQuery(id+"F4.wireOp",EDGE,"E3.left"),sQuery(id+"F4.wireOp",EDGE,"E3.right")])],"isStart":false}),makeQuery(id+"F7.opExtrude","SWEPT_FACE",FACE,{"disambiguationData":[OSD([sQuery(id+"F6.wireOp",EDGE,"E4.left")])]})]}),makeQuery(id+"F26.opExtrude","CAP_FACE",FACE,{"disambiguationData":[OSD([sQuery(id+"F25.wireOp",EDGE,"E31"),sQuery(id+"F25.wireOp",EDGE,"E32"),sQuery(id+"F25.wireOp",EDGE,"E33"),sQuery(id+"F25.wireOp",EDGE,"E34")])],"isStart":true})]});
            var sketch = newSketch(context, id + "F33", { "sketchPlane" : qUnion([Q0])});
            skLineSegment(sketch, "E103.bottom", {"start": v(-192.93, -33.02) * mm, "end": v(-178.27, -33.02) * mm});
            skLineSegment(sketch, "E103.top", {"start": v(-192.93, -40.64) * mm, "end": v(-178.27, -40.64) * mm});
            skLineSegment(sketch, "E103.left", {"start": v(-192.93, -33.02) * mm, "end": v(-192.93, -40.64) * mm});
            skLineSegment(sketch, "E103.right", {"start": v(-178.27, -33.02) * mm, "end": v(-178.27, -40.64) * mm});
            skLineSegment(sketch, "E104.bottom", {"start": v(-130.6, -33.02) * mm, "end": v(-121.7, -33.02) * mm});
            skLineSegment(sketch, "E104.top", {"start": v(-130.6, -40.64) * mm, "end": v(-121.7, -40.64) * mm});
            skLineSegment(sketch, "E104.left", {"start": v(-130.6, -33.02) * mm, "end": v(-130.6, -40.64) * mm});
            skLineSegment(sketch, "E104.right", {"start": v(-121.7, -33.02) * mm, "end": v(-121.7, -40.64) * mm});
            skLineSegment(sketch, "E105.bottom", {"start": v(-69.48, -33.02) * mm, "end": v(-61.11, -33.02) * mm});
            skLineSegment(sketch, "E105.top", {"start": v(-69.48, -40.64) * mm, "end": v(-61.11, -40.64) * mm});
            skLineSegment(sketch, "E105.left", {"start": v(-69.48, -33.02) * mm, "end": v(-69.48, -40.64) * mm});
            skLineSegment(sketch, "E105.right", {"start": v(-61.11, -33.02) * mm, "end": v(-61.11, -40.64) * mm});
            skLineSegment(sketch, "E106.bottom", {"start": v(-4.46, -33.02) * mm, "end": v(4.23, -33.02) * mm});
            skLineSegment(sketch, "E106.top", {"start": v(-4.46, -40.64) * mm, "end": v(4.23, -40.64) * mm});
            skLineSegment(sketch, "E106.left", {"start": v(-4.46, -33.02) * mm, "end": v(-4.46, -40.64) * mm});
            skLineSegment(sketch, "E106.right", {"start": v(4.23, -33.02) * mm, "end": v(4.23, -40.64) * mm});
            skLineSegment(sketch, "E107.bottom", {"start": v(-261.32, -33.02) * mm, "end": v(-252.3, -33.02) * mm});
            skLineSegment(sketch, "E107.top", {"start": v(-261.32, -40.64) * mm, "end": v(-252.3, -40.64) * mm});
            skLineSegment(sketch, "E107.left", {"start": v(-261.32, -33.02) * mm, "end": v(-261.32, -40.64) * mm});
            skLineSegment(sketch, "E107.right", {"start": v(-252.3, -33.02) * mm, "end": v(-252.3, -40.64) * mm});
            skLineSegment(sketch, "E108.bottom", {"start": v(-239.6, -33.02) * mm, "end": v(-231.06, -33.02) * mm});
            skLineSegment(sketch, "E108.top", {"start": v(-239.6, -40.64) * mm, "end": v(-231.06, -40.64) * mm});
            skLineSegment(sketch, "E108.left", {"start": v(-239.6, -33.02) * mm, "end": v(-239.6, -40.64) * mm});
            skLineSegment(sketch, "E108.right", {"start": v(-231.06, -33.02) * mm, "end": v(-231.06, -40.64) * mm});
            skLineSegment(sketch, "E109.bottom", {"start": v(-218.36, -33.02) * mm, "end": v(-205.63, -33.02) * mm});
            skLineSegment(sketch, "E109.top", {"start": v(-218.36, -40.64) * mm, "end": v(-205.63, -40.64) * mm});
            skLineSegment(sketch, "E109.left", {"start": v(-218.36, -33.02) * mm, "end": v(-218.36, -40.64) * mm});
            skLineSegment(sketch, "E109.right", {"start": v(-205.63, -33.02) * mm, "end": v(-205.63, -40.64) * mm});
            skLineSegment(sketch, "E110.bottom", {"start": v(71.5, -33.02) * mm, "end": v(61.03, -33.02) * mm});
            skLineSegment(sketch, "E110.top", {"start": v(71.5, -40.64) * mm, "end": v(61.03, -40.64) * mm});
            skLineSegment(sketch, "E110.left", {"start": v(71.5, -33.02) * mm, "end": v(71.5, -40.64) * mm});
            skLineSegment(sketch, "E110.right", {"start": v(61.03, -33.02) * mm, "end": v(61.03, -40.64) * mm});
            skLineSegment(sketch, "E111.bottom", {"start": v(18.07, -33.02) * mm, "end": v(26.76, -33.02) * mm});
            skLineSegment(sketch, "E111.top", {"start": v(18.07, -40.64) * mm, "end": v(26.76, -40.64) * mm});
            skLineSegment(sketch, "E111.left", {"start": v(18.07, -33.02) * mm, "end": v(18.07, -40.64) * mm});
            skLineSegment(sketch, "E111.right", {"start": v(26.76, -33.02) * mm, "end": v(26.76, -40.64) * mm});
            skLineSegment(sketch, "E112.bottom", {"start": v(38.35, -33.02) * mm, "end": v(48.33, -33.02) * mm});
            skLineSegment(sketch, "E112.top", {"start": v(38.35, -40.64) * mm, "end": v(48.33, -40.64) * mm});
            skLineSegment(sketch, "E112.left", {"start": v(38.35, -33.02) * mm, "end": v(38.35, -40.64) * mm});
            skLineSegment(sketch, "E112.right", {"start": v(48.33, -33.02) * mm, "end": v(48.33, -40.64) * mm});
            skLineSegment(sketch, "E113", {"start": v(-252.3, -40.64) * mm, "end": v(-239.6, -40.64) * mm});
            skLineSegment(sketch, "E114", {"start": v(-231.06, -40.64) * mm, "end": v(-218.36, -40.64) * mm});
            skLineSegment(sketch, "E115", {"start": v(-205.63, -40.64) * mm, "end": v(-192.93, -40.64) * mm});
            skLineSegment(sketch, "E116", {"start": v(-61.11, -40.64) * mm, "end": v(-40.51, -40.64) * mm});
            skLineSegment(sketch, "E117", {"start": v(-30.21, -40.64) * mm, "end": v(-4.46, -40.64) * mm});
            skLineSegment(sketch, "E118", {"start": v(4.23, -40.64) * mm, "end": v(18.07, -40.64) * mm});
            skLineSegment(sketch, "E119", {"start": v(26.76, -40.64) * mm, "end": v(38.35, -40.64) * mm});
            skLineSegment(sketch, "E120", {"start": v(48.33, -40.64) * mm, "end": v(61.03, -40.64) * mm});
            skLineSegment(sketch, "E121.bottom", {"start": v(-110.04, -33.02) * mm, "end": v(-101.35, -33.02) * mm});
            skLineSegment(sketch, "E121.top", {"start": v(-110.04, -40.64) * mm, "end": v(-101.35, -40.64) * mm});
            skLineSegment(sketch, "E121.left", {"start": v(-110.04, -33.02) * mm, "end": v(-110.04, -40.64) * mm});
            skLineSegment(sketch, "E121.right", {"start": v(-101.35, -33.02) * mm, "end": v(-101.35, -40.64) * mm});
            skLineSegment(sketch, "E122.bottom", {"start": v(-91.87, -33.02) * mm, "end": v(-81.07, -33.02) * mm});
            skLineSegment(sketch, "E122.top", {"start": v(-91.87, -40.64) * mm, "end": v(-81.07, -40.64) * mm});
            skLineSegment(sketch, "E122.left", {"start": v(-91.87, -33.02) * mm, "end": v(-91.87, -40.64) * mm});
            skLineSegment(sketch, "E122.right", {"start": v(-81.07, -33.02) * mm, "end": v(-81.07, -40.64) * mm});
            skLineSegment(sketch, "E123.bottom", {"start": v(-171.2, -33.02) * mm, "end": v(-162.5, -33.02) * mm});
            skLineSegment(sketch, "E123.top", {"start": v(-171.2, -40.64) * mm, "end": v(-162.5, -40.64) * mm});
            skLineSegment(sketch, "E123.left", {"start": v(-171.2, -33.02) * mm, "end": v(-171.2, -40.64) * mm});
            skLineSegment(sketch, "E123.right", {"start": v(-162.5, -33.02) * mm, "end": v(-162.5, -40.64) * mm});
            skLineSegment(sketch, "E124.bottom", {"start": v(-150.91, -33.02) * mm, "end": v(-142.87, -33.02) * mm});
            skLineSegment(sketch, "E124.top", {"start": v(-150.91, -40.64) * mm, "end": v(-142.87, -40.64) * mm});
            skLineSegment(sketch, "E124.left", {"start": v(-150.91, -33.02) * mm, "end": v(-150.91, -40.64) * mm});
            skLineSegment(sketch, "E124.right", {"start": v(-142.87, -33.02) * mm, "end": v(-142.87, -40.64) * mm});
            skLineSegment(sketch, "E125.bottom", {"start": v(-48.56, -33.02) * mm, "end": v(-37.94, -33.02) * mm});
            skLineSegment(sketch, "E125.top", {"start": v(-48.56, -40.64) * mm, "end": v(-37.94, -40.64) * mm});
            skLineSegment(sketch, "E125.left", {"start": v(-48.56, -33.02) * mm, "end": v(-48.56, -40.64) * mm});
            skLineSegment(sketch, "E125.right", {"start": v(-37.94, -33.02) * mm, "end": v(-37.94, -40.64) * mm});
            skLineSegment(sketch, "E126.bottom", {"start": v(-27.96, -33.02) * mm, "end": v(-17.34, -33.02) * mm});
            skLineSegment(sketch, "E126.top", {"start": v(-27.96, -40.64) * mm, "end": v(-17.34, -40.64) * mm});
            skLineSegment(sketch, "E126.left", {"start": v(-27.96, -33.02) * mm, "end": v(-27.96, -40.64) * mm});
            skLineSegment(sketch, "E126.right", {"start": v(-17.34, -33.02) * mm, "end": v(-17.34, -40.64) * mm});
            skSolve(sketch);
        }
        {
            var Q0;
            Q0=makeQuery(id+"F33.imprint","IMPRINT",FACE,{"disambiguationData":[TD([[makeQuery(id+"F33.imprint","IMPRINT",EDGE,{"derivedFrom":sQuery(id+"F33.wireOp",EDGE,"E107.bottom")}),-1.0]])]});
            var Q1;
            Q1=makeQuery(id+"F33.imprint","IMPRINT",FACE,{"disambiguationData":[TD([[makeQuery(id+"F33.imprint","IMPRINT",EDGE,{"derivedFrom":sQuery(id+"F33.wireOp",EDGE,"E108.bottom")}),-1.0]])]});
            var Q2;
            Q2=makeQuery(id+"F33.imprint","IMPRINT",FACE,{"disambiguationData":[TD([[makeQuery(id+"F33.imprint","IMPRINT",EDGE,{"derivedFrom":sQuery(id+"F33.wireOp",EDGE,"E109.bottom")}),-1.0]])]});
            var Q3;
            Q3=makeQuery(id+"F33.imprint","IMPRINT",FACE,{"disambiguationData":[TD([[makeQuery(id+"F33.imprint","IMPRINT",EDGE,{"derivedFrom":sQuery(id+"F33.wireOp",EDGE,"E103.bottom")}),-1.0]])]});
            var Q4;
            Q4=makeQuery(id+"F33.imprint","IMPRINT",FACE,{"disambiguationData":[TD([[makeQuery(id+"F33.imprint","IMPRINT",EDGE,{"derivedFrom":sQuery(id+"F33.wireOp",EDGE,"E123.bottom")}),-1.0]])]});
            var Q5;
            Q5=makeQuery(id+"F33.imprint","IMPRINT",FACE,{"disambiguationData":[TD([[makeQuery(id+"F33.imprint","IMPRINT",EDGE,{"derivedFrom":sQuery(id+"F33.wireOp",EDGE,"E124.bottom")}),-1.0]])]});
            var Q6;
            Q6=makeQuery(id+"F33.imprint","IMPRINT",FACE,{"disambiguationData":[TD([[makeQuery(id+"F33.imprint","IMPRINT",EDGE,{"derivedFrom":sQuery(id+"F33.wireOp",EDGE,"E104.bottom")}),-1.0]])]});
            var Q7;
            Q7=makeQuery(id+"F33.imprint","IMPRINT",FACE,{"disambiguationData":[TD([[makeQuery(id+"F33.imprint","IMPRINT",EDGE,{"derivedFrom":sQuery(id+"F33.wireOp",EDGE,"E121.bottom")}),-1.0]])]});
            var Q8;
            Q8=makeQuery(id+"F33.imprint","IMPRINT",FACE,{"disambiguationData":[TD([[makeQuery(id+"F33.imprint","IMPRINT",EDGE,{"derivedFrom":sQuery(id+"F33.wireOp",EDGE,"E122.bottom")}),-1.0]])]});
            var Q9;
            Q9=makeQuery(id+"F33.imprint","IMPRINT",FACE,{"disambiguationData":[TD([[makeQuery(id+"F33.imprint","IMPRINT",EDGE,{"derivedFrom":sQuery(id+"F33.wireOp",EDGE,"E105.bottom")}),-1.0]])]});
            var Q10;
            Q10=makeQuery(id+"F33.imprint","IMPRINT",FACE,{"disambiguationData":[TD([[makeQuery(id+"F33.imprint","IMPRINT",EDGE,{"derivedFrom":sQuery(id+"F33.wireOp",EDGE,"E125.bottom")}),-1.0]])]});
            var Q11;
            Q11=makeQuery(id+"F33.imprint","IMPRINT",FACE,{"disambiguationData":[TD([[makeQuery(id+"F33.imprint","IMPRINT",EDGE,{"derivedFrom":sQuery(id+"F33.wireOp",EDGE,"E126.bottom")}),-1.0]])]});
            var Q12;
            Q12=makeQuery(id+"F33.imprint","IMPRINT",FACE,{"disambiguationData":[TD([[makeQuery(id+"F33.imprint","IMPRINT",EDGE,{"derivedFrom":sQuery(id+"F33.wireOp",EDGE,"E106.bottom")}),-1.0]])]});
            var Q13;
            Q13=makeQuery(id+"F33.imprint","IMPRINT",FACE,{"disambiguationData":[TD([[makeQuery(id+"F33.imprint","IMPRINT",EDGE,{"derivedFrom":sQuery(id+"F33.wireOp",EDGE,"E111.bottom")}),-1.0]])]});
            var Q14;
            Q14=makeQuery(id+"F33.imprint","IMPRINT",FACE,{"disambiguationData":[TD([[makeQuery(id+"F33.imprint","IMPRINT",EDGE,{"derivedFrom":sQuery(id+"F33.wireOp",EDGE,"E110.bottom")}),-1.0]])]});
            var Q15;
            Q15=makeQuery(id+"F33.imprint","IMPRINT",FACE,{"disambiguationData":[TD([[makeQuery(id+"F33.imprint","IMPRINT",EDGE,{"derivedFrom":sQuery(id+"F33.wireOp",EDGE,"E112.bottom")}),-1.0]])]});
            extrude(context, id + "F34", {"entities" : qUnion([Q0, Q1, Q2, Q3, Q4, Q5, Q6, Q7, Q8, Q9, Q10, Q11, Q12, Q13, Q14, Q15]), "oppositeDirection" : true, "depth" : 101.6 * mm, "offsetDistance" : 25.4 * mm});
        }
        {
            var Q0;
            Q0=makeQuery(id+"F7.opExtrude","SWEPT_FACE",FACE,{"disambiguationData":[OSD([sQuery(id+"F6.wireOp",EDGE,"E4.right")])]});
            var sketch = newSketch(context, id + "F35", { "sketchPlane" : qUnion([Q0])});
            skLineSegment(sketch, "E127", {"start": v(-29.08, 46.17) * mm, "end": v(-20.8, 46.17) * mm});
            skLineSegment(sketch, "E128", {"start": v(-20.8, 46.17) * mm, "end": v(-25.56, 38.55) * mm});
            skLineSegment(sketch, "E129", {"start": v(-25.56, 38.55) * mm, "end": v(-34.67, 38.55) * mm});
            skLineSegment(sketch, "E130", {"start": v(-34.67, 38.55) * mm, "end": v(-29.08, 46.17) * mm});
            skSolve(sketch);
        }
        {
            var Q0;
            Q0 = qSketchRegion(id + "F35", true);
            extrude(context, id + "F36", {"entities" : qUnion([Q0]), "operationType" : NewBodyOperationType.ADD, "depth" : 101.6 * mm, "offsetDistance" : 25.4 * mm});
        }
        {
            var Q0;
            Q0=makeQuery(id+"F7.opExtrude","SWEPT_FACE",FACE,{"disambiguationData":[OSD([sQuery(id+"F6.wireOp",EDGE,"E4.right")])]});
            var sketch = newSketch(context, id + "F37", { "sketchPlane" : qUnion([Q0])});
            skLineSegment(sketch, "E131", {"start": v(215.22, 46.17) * mm, "end": v(220.9, 38.55) * mm});
            skLineSegment(sketch, "E132", {"start": v(220.9, 38.55) * mm, "end": v(212.44, 38.55) * mm});
            skLineSegment(sketch, "E133", {"start": v(212.44, 38.55) * mm, "end": v(207.07, 46.17) * mm});
            skLineSegment(sketch, "E134", {"start": v(207.07, 46.17) * mm, "end": v(215.22, 46.17) * mm});
            skSolve(sketch);
        }
        {
            var Q0;
            Q0 = qSketchRegion(id + "F37", true);
            extrude(context, id + "F38", {"entities" : qUnion([Q0]), "operationType" : NewBodyOperationType.ADD, "depth" : 101.6 * mm, "offsetDistance" : 25.4 * mm});
        }
    });
